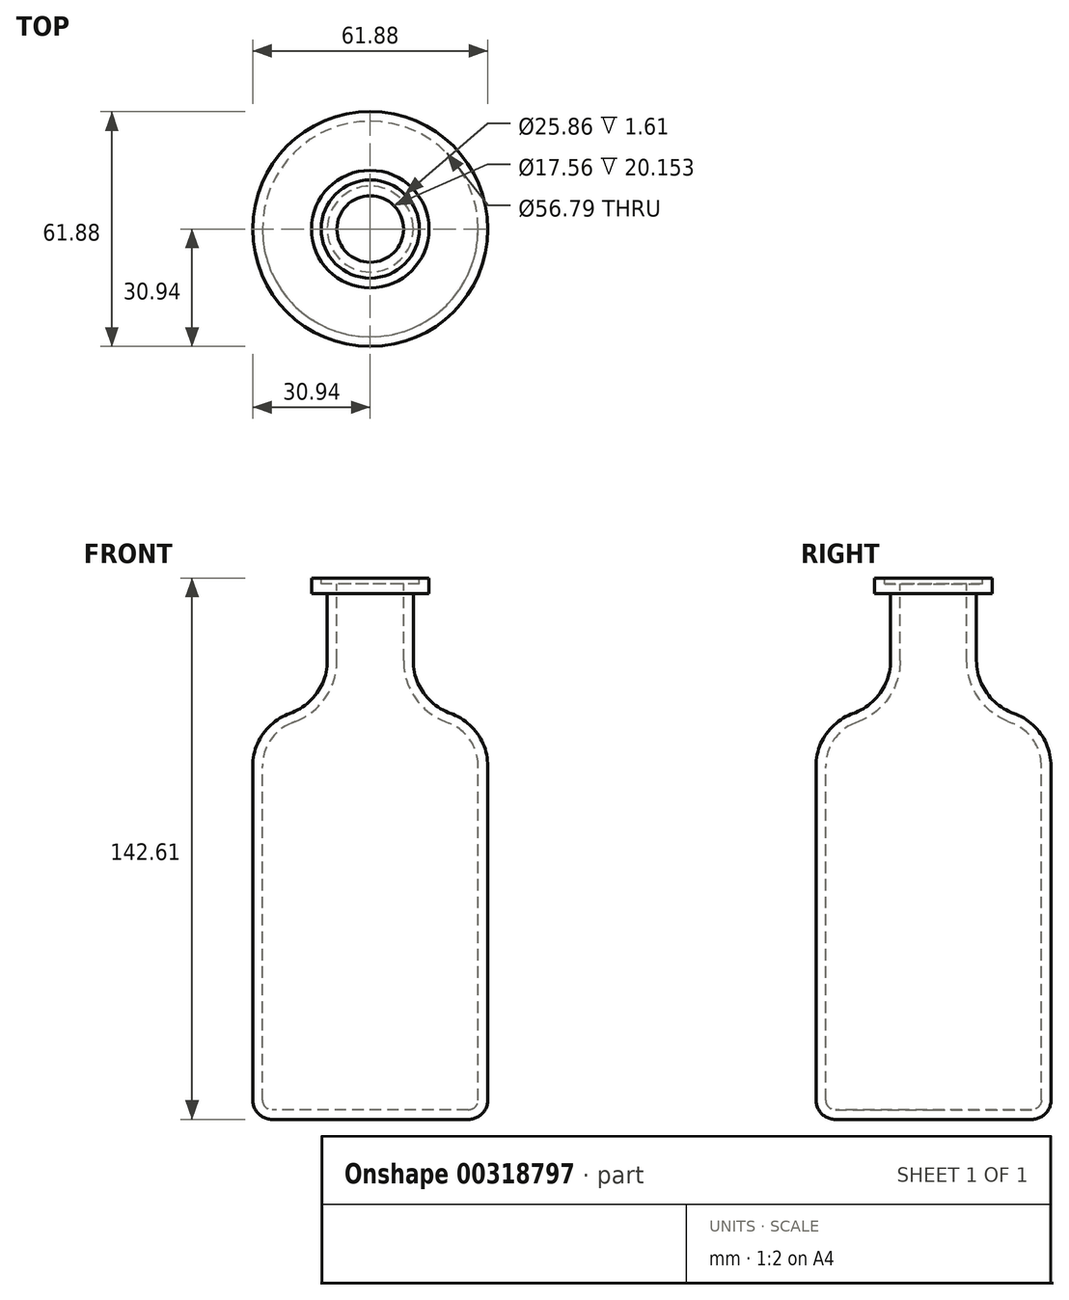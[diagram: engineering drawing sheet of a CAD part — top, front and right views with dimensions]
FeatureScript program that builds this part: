
annotation { "Feature Type Name" : "Feature", "Feature Type Description" : "" }
export const myFeature = defineFeature(function(context is Context, id is Id, definition is map)
    precondition{}
    {
        {
            var Q0;
            Q0=qCreatedBy(makeId("Front.planeOp"),FACE);
            var sketch = newSketch(context, id + "F0", { "sketchPlane" : qUnion([Q0])});
            skLineSegment(sketch, "E0", {"start": v(0, 75.65) * mm, "end": v(0, -76.02) * mm});
            skLineSegment(sketch, "E1", {"start": v(0, -76.02) * mm, "end": v(-30.94, -76.02) * mm});
            skLineSegment(sketch, "E2", {"start": v(-30.94, -76.02) * mm, "end": v(-30.94, 26.98) * mm});
            skLineSegment(sketch, "E3", {"start": v(-30.94, 26.98) * mm, "end": v(-11.32, 34.9) * mm});
            skLineSegment(sketch, "E4", {"start": v(-11.32, 34.9) * mm, "end": v(-11.32, 62.44) * mm});
            skLineSegment(sketch, "E5", {"start": v(-11.32, 62.44) * mm, "end": v(-15.47, 62.44) * mm});
            skLineSegment(sketch, "E6", {"start": v(-15.47, 62.44) * mm, "end": v(-15.47, 66.6) * mm});
            skLineSegment(sketch, "E7", {"start": v(-15.47, 66.6) * mm, "end": v(0, 66.6) * mm});
            skLineSegment(sketch, "E8", {"start": v(0, 66.6) * mm, "end": v(0, -76.02) * mm});
            skSolve(sketch);
        }
        {
            var Q0;
            Q0=makeQuery(id+"F0.imprint","IMPRINT",FACE,{"disambiguationData":[TD([[makeQuery(id+"F0.imprint","IMPRINT",EDGE,{"derivedFrom":sQuery(id+"F0.wireOp",EDGE,"E1")}),-1.0]])]});
            var Q1;
            Q1=sQuery(id+"F0.wireOp",EDGE,"E8");
            revolve(context, id + "F1", {"entities" : qUnion([Q0]), "axis" : qUnion([Q1]), "revolveType" : RevolveType.FULL});
        }
        {
            var Q0;
            Q0=makeQuery(id+"F1.opRevolve","SWEPT_EDGE",EDGE,{"disambiguationData":[OSD([sQuery(id+"F0.wireOp",EDGE,"E2"),sQuery(id+"F0.wireOp",EDGE,"E3")])]});
            var Q1;
            Q1=makeQuery(id+"F1.opRevolve","SWEPT_EDGE",EDGE,{"disambiguationData":[OSD([sQuery(id+"F0.wireOp",EDGE,"E3"),sQuery(id+"F0.wireOp",EDGE,"E4")])]});
            fillet(context, id + "F2", {"entities" : qUnion([Q0, Q1]), "radius" : 14.72 * mm, "tangentPropagation" : true, "allowEdgeOverflow" : false});
        }
        {
            var Q0;
            Q0=makeQuery(id+"F1.opRevolve","SWEPT_EDGE",EDGE,{"disambiguationData":[OSD([sQuery(id+"F0.wireOp",EDGE,"E1"),sQuery(id+"F0.wireOp",EDGE,"E2")])]});
            fillet(context, id + "F3", {"entities" : qUnion([Q0]), "radius" : 5.08 * mm, "tangentPropagation" : true, "allowEdgeOverflow" : false});
        }
        {
            var Q0;
            Q0=makeQuery(id+"F1.opRevolve","SWEPT_FACE",FACE,{"disambiguationData":[OSD([sQuery(id+"F0.wireOp",EDGE,"E7")])]});
            shell(context, id + "F4", {"entities" : qUnion([Q0]), "thickness" : 2.54 * mm});
        }
    });
